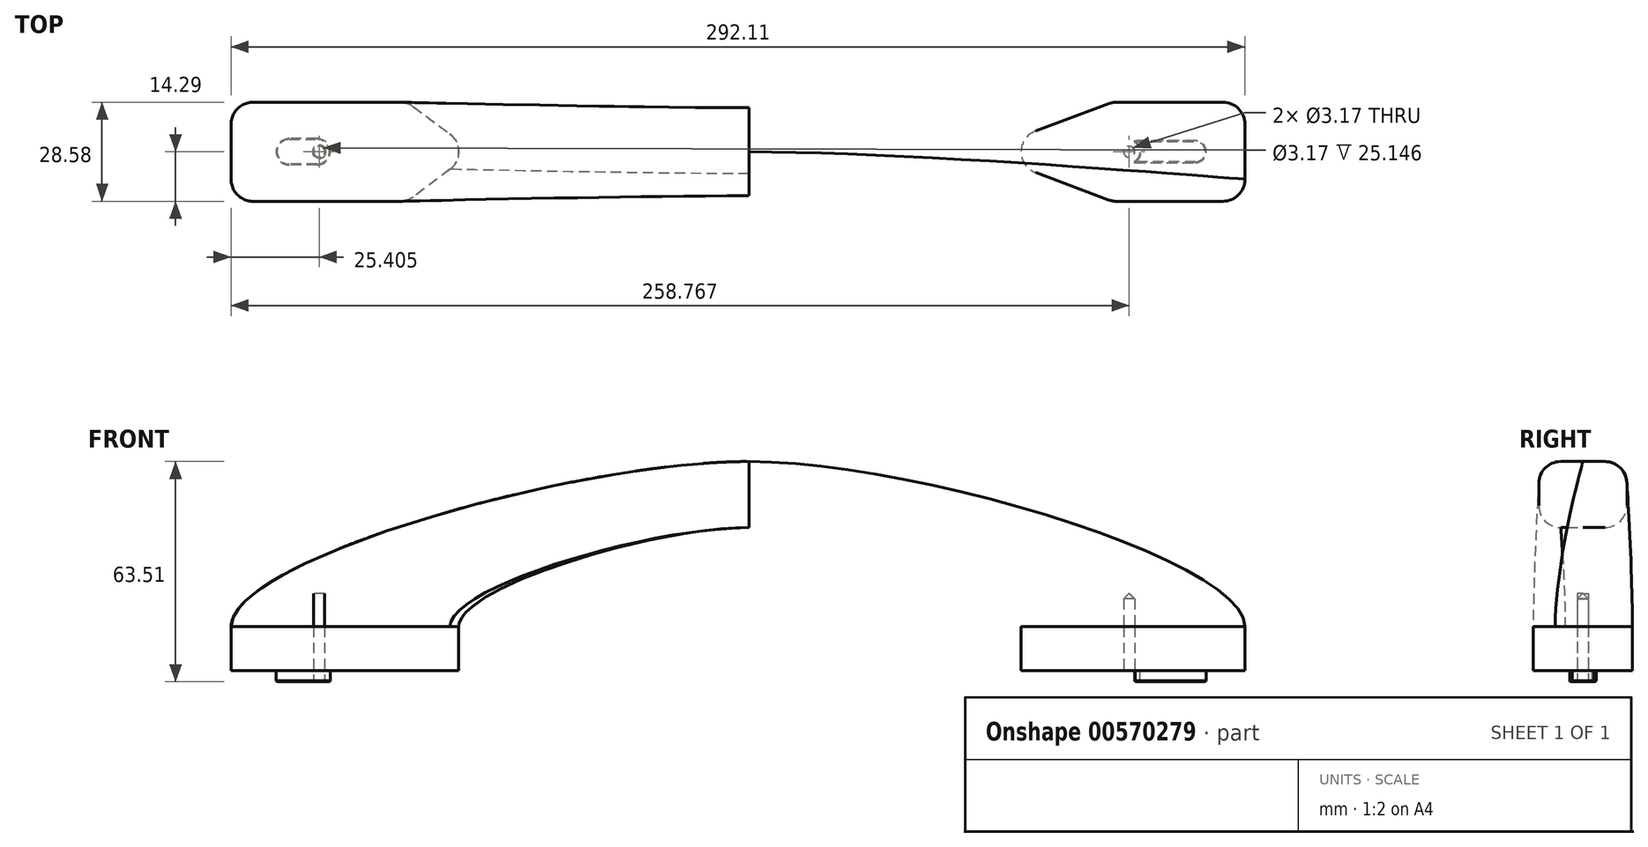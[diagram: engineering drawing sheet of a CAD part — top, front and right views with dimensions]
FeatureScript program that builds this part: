
annotation { "Feature Type Name" : "Feature", "Feature Type Description" : "" }
export const myFeature = defineFeature(function(context is Context, id is Id, definition is map)
    precondition{}
    {
        {
            var Q0;
            Q0=qCreatedBy(makeId("Top.planeOp"),FACE);
            var sketch = newSketch(context, id + "F0", { "sketchPlane" : qUnion([Q0])});
            skLineSegment(sketch, "E0.bottom", {"start": v(-100.54, -14.29) * mm, "end": v(-142.88, -14.29) * mm});
            skLineSegment(sketch, "E0.top", {"start": v(-100.54, 14.29) * mm, "end": v(-142.88, 14.29) * mm});
            skLineSegment(sketch, "E0.left", {"start": v(-98.42, -14.29) * mm, "end": v(-98.42, 14.29) * mm, "construction": true});
            skLineSegment(sketch, "E0.right", {"start": v(-149.23, -7.94) * mm, "end": v(-149.23, 7.94) * mm});
            skPoint(sketch, "E0.middle", {"position": v(-123.83, 0) * mm});
            skLineSegment(sketch, "E1", {"start": v(0, 0) * mm, "end": v(0, 50.83) * mm, "construction": true});
            skLineSegment(sketch, "E2.bottom", {"start": v(136.53, -14.29) * mm, "end": v(105.93, -14.29) * mm, "construction": true});
            skLineSegment(sketch, "E2.top", {"start": v(136.53, 14.29) * mm, "end": v(105.93, 14.29) * mm, "construction": true});
            skLineSegment(sketch, "E2.left", {"start": v(142.88, -7.94) * mm, "end": v(142.88, 7.94) * mm, "construction": true});
            skLineSegment(sketch, "E2.right", {"start": v(104.78, -14.29) * mm, "end": v(104.78, 14.29) * mm, "construction": true});
            skPoint(sketch, "E2.middle", {"position": v(123.83, 0) * mm});
            skLineSegment(sketch, "E3", {"start": v(103.7, 13.88) * mm, "end": v(82.53, 5.95) * mm, "construction": true});
            skLineSegment(sketch, "E4", {"start": v(82.53, -5.95) * mm, "end": v(103.7, -13.88) * mm, "construction": true});
            skPoint(sketch, "E5.visualSharp", {"position": v(66.68, 0) * mm});
            skArc(sketch, "E5.filletArc", {"start": v(82.53, 5.95) * mm, "mid": v(78.4, 0) * mm, "end": v(82.53, -5.95) * mm, "construction": true});
            skLineSegment(sketch, "E6", {"start": v(-96.73, 13.02) * mm, "end": v(-86.15, 5.08) * mm});
            skLineSegment(sketch, "E7", {"start": v(-86.15, -5.08) * mm, "end": v(-96.73, -13.02) * mm});
            skPoint(sketch, "E8.visualSharp", {"position": v(-79.38, 0) * mm});
            skArc(sketch, "E8.filletArc", {"start": v(-86.15, -5.08) * mm, "mid": v(-83.6, 0) * mm, "end": v(-86.15, 5.08) * mm});
            skPoint(sketch, "E9.visualSharp", {"position": v(-149.23, 14.29) * mm});
            skArc(sketch, "E9.filletArc", {"start": v(-142.88, 14.29) * mm, "mid": v(-147.37, 12.43) * mm, "end": v(-149.23, 7.94) * mm});
            skPoint(sketch, "E10.visualSharp", {"position": v(-149.23, -14.29) * mm});
            skArc(sketch, "E10.filletArc", {"start": v(-149.23, -7.94) * mm, "mid": v(-147.37, -12.43) * mm, "end": v(-142.88, -14.29) * mm});
            skPoint(sketch, "E11.visualSharp", {"position": v(142.88, 14.29) * mm});
            skArc(sketch, "E11.filletArc", {"start": v(142.88, 7.94) * mm, "mid": v(141.02, 12.43) * mm, "end": v(136.53, 14.29) * mm, "construction": true});
            skPoint(sketch, "E12.visualSharp", {"position": v(142.88, -14.29) * mm});
            skArc(sketch, "E12.filletArc", {"start": v(136.53, -14.29) * mm, "mid": v(141.02, -12.43) * mm, "end": v(142.88, -7.94) * mm, "construction": true});
            skPoint(sketch, "E13.visualSharp", {"position": v(104.78, -14.29) * mm});
            skArc(sketch, "E13.filletArc", {"start": v(103.7, -13.88) * mm, "mid": v(104.8, -14.19) * mm, "end": v(105.93, -14.29) * mm});
            skPoint(sketch, "E14.visualSharp", {"position": v(104.78, 14.29) * mm});
            skArc(sketch, "E14.filletArc", {"start": v(105.93, 14.29) * mm, "mid": v(104.8, 14.19) * mm, "end": v(103.7, 13.88) * mm, "construction": true});
            skPoint(sketch, "E15.visualSharp", {"position": v(-98.43, 14.29) * mm});
            skArc(sketch, "E15.filletArc", {"start": v(-96.73, 13.02) * mm, "mid": v(-98.53, 13.96) * mm, "end": v(-100.54, 14.29) * mm});
            skPoint(sketch, "E16.visualSharp", {"position": v(-98.43, -14.29) * mm});
            skArc(sketch, "E16.filletArc", {"start": v(-100.54, -14.29) * mm, "mid": v(-98.53, -13.96) * mm, "end": v(-96.73, -13.02) * mm});
            skSolve(sketch);
        }
        {
            var Q0;
            Q0=qCreatedBy(makeId("Front.planeOp"),FACE);
            var sketch = newSketch(context, id + "F1", { "sketchPlane" : qUnion([Q0])});
            skLineSegment(sketch, "E17", {"start": v(-123.83, 0) * mm, "end": v(-123.83, 25.4) * mm});
            skLineSegment(sketch, "E18", {"start": v(0, 0) * mm, "end": v(0, 50.8) * mm, "construction": true});
            skPoint(sketch, "E19.start.orphan", {"position": v(123.83, 0) * mm});
            skArc(sketch, "E20", {"start": v(0, 50.8) * mm, "mid": v(-62.89, 42.84) * mm, "end": v(-123.82, 25.4) * mm});
            skSolve(sketch);
        }
        {
            var Q0;
            Q0=qCreatedBy(makeId("Top.planeOp"),FACE);
            var sketch = newSketch(context, id + "F2", { "sketchPlane" : qUnion([Q0])});
            skLineSegment(sketch, "E21.0", {"start": v(103.7, 13.88) * mm, "end": v(82.53, 5.95) * mm});
            skArc(sketch, "E21.1", {"start": v(105.93, 14.29) * mm, "mid": v(104.8, 14.19) * mm, "end": v(103.7, 13.88) * mm});
            skLineSegment(sketch, "E21.2", {"start": v(136.53, 14.29) * mm, "end": v(105.93, 14.29) * mm});
            skLineSegment(sketch, "E21.3", {"start": v(104.78, -14.29) * mm, "end": v(104.78, 14.29) * mm, "construction": true});
            skArc(sketch, "E21.4", {"start": v(103.7, -13.88) * mm, "mid": v(104.8, -14.19) * mm, "end": v(105.93, -14.29) * mm});
            skLineSegment(sketch, "E21.5", {"start": v(82.53, -5.95) * mm, "end": v(103.7, -13.88) * mm});
            skLineSegment(sketch, "E21.6", {"start": v(136.53, -14.29) * mm, "end": v(105.93, -14.29) * mm});
            skArc(sketch, "E21.7", {"start": v(82.53, 5.95) * mm, "mid": v(78.4, 0) * mm, "end": v(82.53, -5.95) * mm});
            skArc(sketch, "E21.8", {"start": v(142.88, 7.94) * mm, "mid": v(141.02, 12.43) * mm, "end": v(136.53, 14.29) * mm});
            skArc(sketch, "E21.9", {"start": v(136.53, -14.29) * mm, "mid": v(141.02, -12.43) * mm, "end": v(142.88, -7.94) * mm});
            skLineSegment(sketch, "E21.10", {"start": v(142.88, -7.94) * mm, "end": v(142.88, 7.94) * mm});
            skSolve(sketch);
        }
        {
            var Q0;
            Q0=qCreatedBy(makeId("Front.planeOp"),FACE);
            var sketch = newSketch(context, id + "F3", { "sketchPlane" : qUnion([Q0])});
            skLineSegment(sketch, "E22.1", {"start": v(-123.83, 0) * mm, "end": v(-123.83, 25.4) * mm});
            skLineSegment(sketch, "E23.MirrorCS", {"start": v(123.83, 0) * mm, "end": v(123.83, 25.4) * mm});
            skArc(sketch, "E24", {"start": v(123.83, 25.4) * mm, "mid": v(0, 50.8) * mm, "end": v(-123.83, 25.4) * mm});
            skSolve(sketch);
        }
        {
            var Q0;
            Q0=makeQuery(id+"F0.imprint","IMPRINT",FACE,{"disambiguationData":[TD([[makeQuery(id+"F0.imprint","IMPRINT",EDGE,{"derivedFrom":sQuery(id+"F0.wireOp",EDGE,"E0.bottom")}),-1.0]])]});
            extrude(context, id + "F4", {"entities" : qUnion([Q0]), "depth" : 12.7 * mm, "offsetDistance" : 25.4 * mm});
        }
        {
            var Q0;
            Q0=makeQuery(id+"F2.imprint","IMPRINT",FACE,{"disambiguationData":[TD([[makeQuery(id+"F2.imprint","IMPRINT",EDGE,{"derivedFrom":sQuery(id+"F2.wireOp",EDGE,"E21.0")}),1.0]])]});
            extrude(context, id + "F5", {"entities" : qUnion([Q0]), "depth" : 12.7 * mm, "offsetDistance" : 25.4 * mm});
        }
        {
            var Q0;
            Q0=qCreatedBy(makeId("Right.planeOp"),FACE);
            var sketch = newSketch(context, id + "F6", { "sketchPlane" : qUnion([Q0])});
            skLineSegment(sketch, "E25.bottom", {"start": v(-6.35, 41.27) * mm, "end": v(6.35, 41.27) * mm});
            skLineSegment(sketch, "E25.top", {"start": v(-6.35, 60.32) * mm, "end": v(6.35, 60.32) * mm});
            skLineSegment(sketch, "E25.left", {"start": v(-12.7, 47.62) * mm, "end": v(-12.7, 53.97) * mm});
            skLineSegment(sketch, "E25.right", {"start": v(12.7, 47.62) * mm, "end": v(12.7, 53.97) * mm});
            skPoint(sketch, "E25.middle", {"position": v(0, 50.8) * mm});
            skPoint(sketch, "E26.visualSharp", {"position": v(12.7, 60.32) * mm});
            skArc(sketch, "E26.filletArc", {"start": v(12.7, 53.97) * mm, "mid": v(10.84, 58.47) * mm, "end": v(6.35, 60.32) * mm});
            skPoint(sketch, "E27.visualSharp", {"position": v(-12.7, 60.32) * mm});
            skArc(sketch, "E27.filletArc", {"start": v(-6.35, 60.32) * mm, "mid": v(-10.84, 58.47) * mm, "end": v(-12.7, 53.97) * mm});
            skPoint(sketch, "E28.visualSharp", {"position": v(-12.7, 41.27) * mm});
            skArc(sketch, "E28.filletArc", {"start": v(-12.7, 47.62) * mm, "mid": v(-10.84, 43.13) * mm, "end": v(-6.35, 41.27) * mm});
            skPoint(sketch, "E29.visualSharp", {"position": v(12.7, 41.27) * mm});
            skArc(sketch, "E29.filletArc", {"start": v(6.35, 41.27) * mm, "mid": v(10.84, 43.13) * mm, "end": v(12.7, 47.62) * mm});
            skSolve(sketch);
        }
        {
            var Q1;
            Q1=makeQuery(id+"F6.imprint","IMPRINT",FACE,{"disambiguationData":[TD([[makeQuery(id+"F6.imprint","IMPRINT",EDGE,{"derivedFrom":sQuery(id+"F6.wireOp",EDGE,"E25.bottom")}),1.0]])]});
            var Q2;
            Q2=makeQuery(id+"F4.opExtrude","CAP_FACE",FACE,{"disambiguationData":[OSD([sQuery(id+"F0.wireOp",EDGE,"E0.bottom"),sQuery(id+"F0.wireOp",EDGE,"E0.top"),sQuery(id+"F0.wireOp",EDGE,"E0.right"),sQuery(id+"F0.wireOp",EDGE,"E6"),sQuery(id+"F0.wireOp",EDGE,"E7"),sQuery(id+"F0.wireOp",EDGE,"E8.filletArc"),sQuery(id+"F0.wireOp",EDGE,"E9.filletArc"),sQuery(id+"F0.wireOp",EDGE,"E10.filletArc"),sQuery(id+"F0.wireOp",EDGE,"E15.filletArc"),sQuery(id+"F0.wireOp",EDGE,"E16.filletArc")])],"isStart":false});
            var Q3;
            Q3=sQuery(id+"F3.wireOp",EDGE,"E22.0");
            var Q4;
            Q4=sQuery(id+"F6.wireOp",VERTEX,"E25.middle");
            var Q5;
            Q5=sQuery(id+"F3.wireOp",VERTEX,"E22.1.end");
            loft(context, id + "F7", {"operationType" : NewBodyOperationType.ADD, "startCondition" : LoftEndDerivativeType.NORMAL_TO_PROFILE, "startMagnitude" : 1, "endCondition" : LoftEndDerivativeType.NORMAL_TO_PROFILE, "endMagnitude" : 1, "sheetProfilesArray" : [{ "sheetProfileEntities" : qUnion([Q1]) }, { "sheetProfileEntities" : qUnion([Q2]) }], "guidesArray" : [{ "guideEntities" : qUnion([Q3]), "guideDerivativeType" : LoftGuideDerivativeType.DEFAULT, "guideDerivativeMagnitude" : 1 }], "connections" : [{ "connectionEntities" : qUnion([Q4, Q5]), "connectionEdgeQueries" : qUnion([]), "connectionEdgeParameters" : [] }]});
        }
        {
            var Q0;
            Q0=makeQuery(id+"F7.opLoft","CAP_FACE",FACE,{"disambiguationData":[OSD([makeQuery(id+"F6.imprint","IMPRINT",FACE,{"disambiguationData":[TD([[makeQuery(id+"F6.imprint","IMPRINT",EDGE,{"derivedFrom":sQuery(id+"F6.wireOp",EDGE,"E25.bottom")}),1.0]])]})])],"isStart":true});
            var Q1;
            Q1=makeQuery(id+"F5.opExtrude","CAP_FACE",FACE,{"disambiguationData":[OSD([sQuery(id+"F2.wireOp",EDGE,"E21.0"),sQuery(id+"F2.wireOp",EDGE,"E21.1"),sQuery(id+"F2.wireOp",EDGE,"E21.2"),sQuery(id+"F2.wireOp",EDGE,"E21.4"),sQuery(id+"F2.wireOp",EDGE,"E21.5"),sQuery(id+"F2.wireOp",EDGE,"E21.6"),sQuery(id+"F2.wireOp",EDGE,"E21.7"),sQuery(id+"F2.wireOp",EDGE,"E21.8"),sQuery(id+"F2.wireOp",EDGE,"E21.9"),sQuery(id+"F2.wireOp",EDGE,"E21.10")])],"isStart":false});
            loft(context, id + "F8", {"startCondition" : LoftEndDerivativeType.NORMAL_TO_PROFILE, "startMagnitude" : 1, "endCondition" : LoftEndDerivativeType.NORMAL_TO_PROFILE, "endMagnitude" : 1, "sheetProfilesArray" : [{ "sheetProfileEntities" : qUnion([Q0]) }, { "sheetProfileEntities" : qUnion([Q1]) }]});
        }
        {
            var Q0;
            Q0=makeQuery(id+"F2.imprint","IMPRINT",FACE,{"disambiguationData":[TD([[makeQuery(id+"F2.imprint","IMPRINT",EDGE,{"derivedFrom":sQuery(id+"F2.wireOp",EDGE,"E21.0")}),1.0]])]});
            var sketch = newSketch(context, id + "F9", { "sketchPlane" : qUnion([Q0])});
            skCircle(sketch, "E30", {"center": v(109.54, 0) * mm, "radius": 1.59 * mm});
            skCircle(sketch, "E31", {"center": v(-123.83, 0) * mm, "radius": 1.59 * mm});
            skSolve(sketch);
        }
        {
            var Q0;
            Q0=makeQuery(id+"F9.imprint","IMPRINT",FACE,{"disambiguationData":[TD([[makeQuery(id+"F9.imprint","IMPRINT",EDGE,{"derivedFrom":sQuery(id+"F9.wireOp",EDGE,"E31")}),1.0]])]});
            var Q1;
            Q1=makeQuery(id+"F9.imprint","IMPRINT",FACE,{"disambiguationData":[TD([[makeQuery(id+"F9.imprint","IMPRINT",EDGE,{"derivedFrom":sQuery(id+"F9.wireOp",EDGE,"E30")}),1.0]])]});
            extrude(context, id + "F10", {"entities" : qUnion([Q0, Q1]), "operationType" : NewBodyOperationType.REMOVE, "depth" : 22.22 * mm, "offsetDistance" : 25.4 * mm});
        }
        {
            var Q0;
            Q0=makeQuery(id+"F4.opExtrude","CAP_FACE",FACE,{"disambiguationData":[OSD([sQuery(id+"F0.wireOp",EDGE,"E0.bottom"),sQuery(id+"F0.wireOp",EDGE,"E0.top"),sQuery(id+"F0.wireOp",EDGE,"E0.right"),sQuery(id+"F0.wireOp",EDGE,"E6"),sQuery(id+"F0.wireOp",EDGE,"E7"),sQuery(id+"F0.wireOp",EDGE,"E8.filletArc"),sQuery(id+"F0.wireOp",EDGE,"E9.filletArc"),sQuery(id+"F0.wireOp",EDGE,"E10.filletArc"),sQuery(id+"F0.wireOp",EDGE,"E15.filletArc"),sQuery(id+"F0.wireOp",EDGE,"E16.filletArc")])],"isStart":true});
            var sketch = newSketch(context, id + "F11", { "sketchPlane" : qUnion([Q0])});
            skLineSegment(sketch, "E32", {"start": v(-123.83, 0) * mm, "end": v(-136.2, 0) * mm, "construction": true});
            skLineSegment(sketch, "E33.0", {"start": v(-124.46, -3.8) * mm, "end": v(-132.4, -3.81) * mm});
            skLineSegment(sketch, "E34.0", {"start": v(-124.46, 3.81) * mm, "end": v(-132.4, 3.8) * mm});
            skArc(sketch, "E35", {"start": v(-132.4, 3.8) * mm, "mid": v(-136.2, 0) * mm, "end": v(-132.4, -3.81) * mm});
            skArc(sketch, "E36", {"start": v(-124.46, -3.8) * mm, "mid": v(-120.65, 0) * mm, "end": v(-124.46, 3.8) * mm});
            skSolve(sketch);
        }
        {
            var Q0;
            Q0=makeQuery(id+"F11.imprint","IMPRINT",FACE,{"disambiguationData":[TD([[makeQuery(id+"F11.imprint","IMPRINT",EDGE,{"derivedFrom":sQuery(id+"F11.wireOp",EDGE,"E33.0")}),-1.0]])]});
            extrude(context, id + "F12", {"entities" : qUnion([Q0]), "operationType" : NewBodyOperationType.ADD, "depth" : 3.17 * mm, "offsetDistance" : 25.4 * mm});
        }
        {
            var Q0;
            Q0=makeQuery(id+"F2.imprint","IMPRINT",FACE,{"disambiguationData":[TD([[makeQuery(id+"F2.imprint","IMPRINT",EDGE,{"derivedFrom":sQuery(id+"F2.wireOp",EDGE,"E21.0")}),1.0]])]});
            var sketch = newSketch(context, id + "F13", { "sketchPlane" : qUnion([Q0])});
            skCircle(sketch, "E37.0", {"center": v(109.54, 0) * mm, "radius": 1.59 * mm, "construction": true});
            skArc(sketch, "E38", {"start": v(109.54, -3.18) * mm, "mid": v(112.71, 0) * mm, "end": v(109.54, 3.17) * mm});
            skLineSegment(sketch, "E39", {"start": v(106.36, 0) * mm, "end": v(131.76, 0) * mm, "construction": true});
            skLineSegment(sketch, "E40", {"start": v(109.54, 0) * mm, "end": v(109.54, -10.63) * mm, "construction": true});
            skLineSegment(sketch, "E41", {"start": v(128.59, -10.63) * mm, "end": v(128.59, 0) * mm, "construction": true});
            skLineSegment(sketch, "E42", {"start": v(109.54, -3.18) * mm, "end": v(128.59, -3.17) * mm});
            skPoint(sketch, "E42.startSnap0", {"position": v(109.54, -5.31) * mm});
            skLineSegment(sketch, "E43.MirrorCS", {"start": v(109.54, 3.18) * mm, "end": v(128.59, 3.17) * mm});
            skArc(sketch, "E44", {"start": v(125.41, 0) * mm, "mid": v(126.34, -2.25) * mm, "end": v(128.59, -3.17) * mm, "construction": true});
            skArc(sketch, "E45", {"start": v(128.59, -3.17) * mm, "mid": v(131.76, 0) * mm, "end": v(128.59, 3.18) * mm});
            skArc(sketch, "E46", {"start": v(128.59, 3.18) * mm, "mid": v(126.34, 2.25) * mm, "end": v(125.41, 0) * mm, "construction": true});
            skSolve(sketch);
        }
        {
            var Q0;
            Q0 = qSketchRegion(id + "F13", true);
            extrude(context, id + "F14", {"entities" : qUnion([Q0]), "operationType" : NewBodyOperationType.ADD, "oppositeDirection" : true, "depth" : 3.17 * mm, "offsetDistance" : 25.4 * mm});
        }
        {
            var Q0;
            Q0=makeQuery(id+"F12.opExtrude","CAP_EDGE",EDGE,{"disambiguationData":[OSD([sQuery(id+"F9.wireOp",EDGE,"E31")])],"isStart":false});
            chamfer(context, id + "F15", {"entities" : qUnion([Q0]), "width" : 0.25 * mm, "tangentPropagation" : true});
        }
        {
            var Q0;
            Q0=makeQuery(id+"F14.opExtrude","CAP_EDGE",EDGE,{"disambiguationData":[OSD([sQuery(id+"F13.wireOp",EDGE,"E38")])],"isStart":false});
            var Q1;
            Q1=makeQuery(id+"F14.opExtrude","CAP_FACE",FACE,{"disambiguationData":[OSD([sQuery(id+"F13.wireOp",EDGE,"E38"),sQuery(id+"F13.wireOp",EDGE,"E42"),sQuery(id+"F13.wireOp",EDGE,"E43.MirrorCS"),sQuery(id+"F13.wireOp",EDGE,"E45")])],"isStart":false});
            var Q2;
            Q2=makeQuery(id+"F14.opExtrude","SWEPT_EDGE",EDGE,{"disambiguationData":[OSD([sQuery(id+"F13.wireOp",EDGE,"E38"),sQuery(id+"F13.wireOp",EDGE,"E42")])]});
            var Q3;
            Q3=makeQuery(id+"F14.opExtrude","SWEPT_EDGE",EDGE,{"disambiguationData":[OSD([sQuery(id+"F13.wireOp",EDGE,"E38"),sQuery(id+"F13.wireOp",EDGE,"E43.MirrorCS")])]});
            var Q4;
            Q4=makeQuery(id+"F10.boolean.opBoolean","COPY",EDGE,{"derivedFrom":makeQuery(id+"F10.opExtrude","CAP_EDGE",EDGE,{"disambiguationData":[OSD([sQuery(id+"F9.wireOp",EDGE,"E30")])],"isStart":true})});
            chamfer(context, id + "F16", {"entities" : qUnion([Q0, Q1, Q2, Q3, Q4]), "width" : 0.25 * mm, "tangentPropagation" : true});
        }
        {
            var Q0;
            Q0=makeQuery(id+"F10.boolean.opBoolean","COPY",FACE,{"derivedFrom":makeQuery(id+"F10.opExtrude","CAP_FACE",FACE,{"disambiguationData":[OSD([sQuery(id+"F9.wireOp",EDGE,"E30")])],"isStart":false})});
            var Q1;
            Q1=makeQuery(id+"F10.opExtrude","CAP_FACE",FACE,{"disambiguationData":[OSD([sQuery(id+"F9.wireOp",EDGE,"E31")])],"isStart":false});
            chamfer(context, id + "F17", {"entities" : qUnion([Q0, Q1]), "width" : 1.52 * mm, "tangentPropagation" : true});
        }
        {
            var Q0;
            Q0=makeQuery(id+"F12.opExtrude","CAP_FACE",FACE,{"disambiguationData":[OSD([sQuery(id+"F9.wireOp",EDGE,"E31"),sQuery(id+"F11.wireOp",EDGE,"E33.0"),sQuery(id+"F11.wireOp",EDGE,"E34.0"),sQuery(id+"F11.wireOp",EDGE,"E35"),sQuery(id+"F11.wireOp",EDGE,"E36")])],"isStart":false});
            chamfer(context, id + "F18", {"entities" : qUnion([Q0]), "width" : 0.25 * mm, "tangentPropagation" : true});
        }
        {
            var Q0;
            Q0=makeQuery(id+"F14.opExtrude","CAP_EDGE",EDGE,{"disambiguationData":[OSD([sQuery(id+"F13.wireOp",EDGE,"E42")])],"isStart":true});
            var Q1;
            Q1=makeQuery(id+"F14.opExtrude","CAP_EDGE",EDGE,{"disambiguationData":[OSD([sQuery(id+"F13.wireOp",EDGE,"E38")])],"isStart":true});
            var Q2;
            Q2=makeQuery(id+"F16.opChamfer","BLEND_EDGE",EDGE,{"blendedFrom":[makeQuery(id+"F14.opExtrude","SWEPT_EDGE",EDGE,{"disambiguationData":[OSD([sQuery(id+"F13.wireOp",EDGE,"E38"),sQuery(id+"F13.wireOp",EDGE,"E42")])]}),makeQuery(id+"F5.opExtrude","CAP_FACE",FACE,{"disambiguationData":[OSD([sQuery(id+"F2.wireOp",EDGE,"E21.0"),sQuery(id+"F2.wireOp",EDGE,"E21.1"),sQuery(id+"F2.wireOp",EDGE,"E21.2"),sQuery(id+"F2.wireOp",EDGE,"E21.4"),sQuery(id+"F2.wireOp",EDGE,"E21.5"),sQuery(id+"F2.wireOp",EDGE,"E21.6"),sQuery(id+"F2.wireOp",EDGE,"E21.7"),sQuery(id+"F2.wireOp",EDGE,"E21.8"),sQuery(id+"F2.wireOp",EDGE,"E21.9"),sQuery(id+"F2.wireOp",EDGE,"E21.10")])],"isStart":true})],"blendedInto":[makeQuery(id+"F5.opExtrude","CAP_FACE",FACE,{"disambiguationData":[OSD([sQuery(id+"F2.wireOp",EDGE,"E21.0"),sQuery(id+"F2.wireOp",EDGE,"E21.1"),sQuery(id+"F2.wireOp",EDGE,"E21.2"),sQuery(id+"F2.wireOp",EDGE,"E21.4"),sQuery(id+"F2.wireOp",EDGE,"E21.5"),sQuery(id+"F2.wireOp",EDGE,"E21.6"),sQuery(id+"F2.wireOp",EDGE,"E21.7"),sQuery(id+"F2.wireOp",EDGE,"E21.8"),sQuery(id+"F2.wireOp",EDGE,"E21.9"),sQuery(id+"F2.wireOp",EDGE,"E21.10")])],"isStart":true})]});
            var Q3;
            Q3=makeQuery(id+"F16.opChamfer","BLEND_EDGE",EDGE,{"blendedFrom":[makeQuery(id+"F14.opExtrude","SWEPT_EDGE",EDGE,{"disambiguationData":[OSD([sQuery(id+"F13.wireOp",EDGE,"E38"),sQuery(id+"F13.wireOp",EDGE,"E43.MirrorCS")])]}),makeQuery(id+"F5.opExtrude","CAP_FACE",FACE,{"disambiguationData":[OSD([sQuery(id+"F2.wireOp",EDGE,"E21.0"),sQuery(id+"F2.wireOp",EDGE,"E21.1"),sQuery(id+"F2.wireOp",EDGE,"E21.2"),sQuery(id+"F2.wireOp",EDGE,"E21.4"),sQuery(id+"F2.wireOp",EDGE,"E21.5"),sQuery(id+"F2.wireOp",EDGE,"E21.6"),sQuery(id+"F2.wireOp",EDGE,"E21.7"),sQuery(id+"F2.wireOp",EDGE,"E21.8"),sQuery(id+"F2.wireOp",EDGE,"E21.9"),sQuery(id+"F2.wireOp",EDGE,"E21.10")])],"isStart":true})],"blendedInto":[makeQuery(id+"F5.opExtrude","CAP_FACE",FACE,{"disambiguationData":[OSD([sQuery(id+"F2.wireOp",EDGE,"E21.0"),sQuery(id+"F2.wireOp",EDGE,"E21.1"),sQuery(id+"F2.wireOp",EDGE,"E21.2"),sQuery(id+"F2.wireOp",EDGE,"E21.4"),sQuery(id+"F2.wireOp",EDGE,"E21.5"),sQuery(id+"F2.wireOp",EDGE,"E21.6"),sQuery(id+"F2.wireOp",EDGE,"E21.7"),sQuery(id+"F2.wireOp",EDGE,"E21.8"),sQuery(id+"F2.wireOp",EDGE,"E21.9"),sQuery(id+"F2.wireOp",EDGE,"E21.10")])],"isStart":true})]});
            var Q4;
            Q4=makeQuery(id+"F12.opExtrude","CAP_EDGE",EDGE,{"disambiguationData":[OSD([sQuery(id+"F11.wireOp",EDGE,"E33.0")])],"isStart":true});
            chamfer(context, id + "F19", {"entities" : qUnion([Q0, Q1, Q2, Q3, Q4]), "width" : 0.25 * mm, "tangentPropagation" : true});
        }
    });
